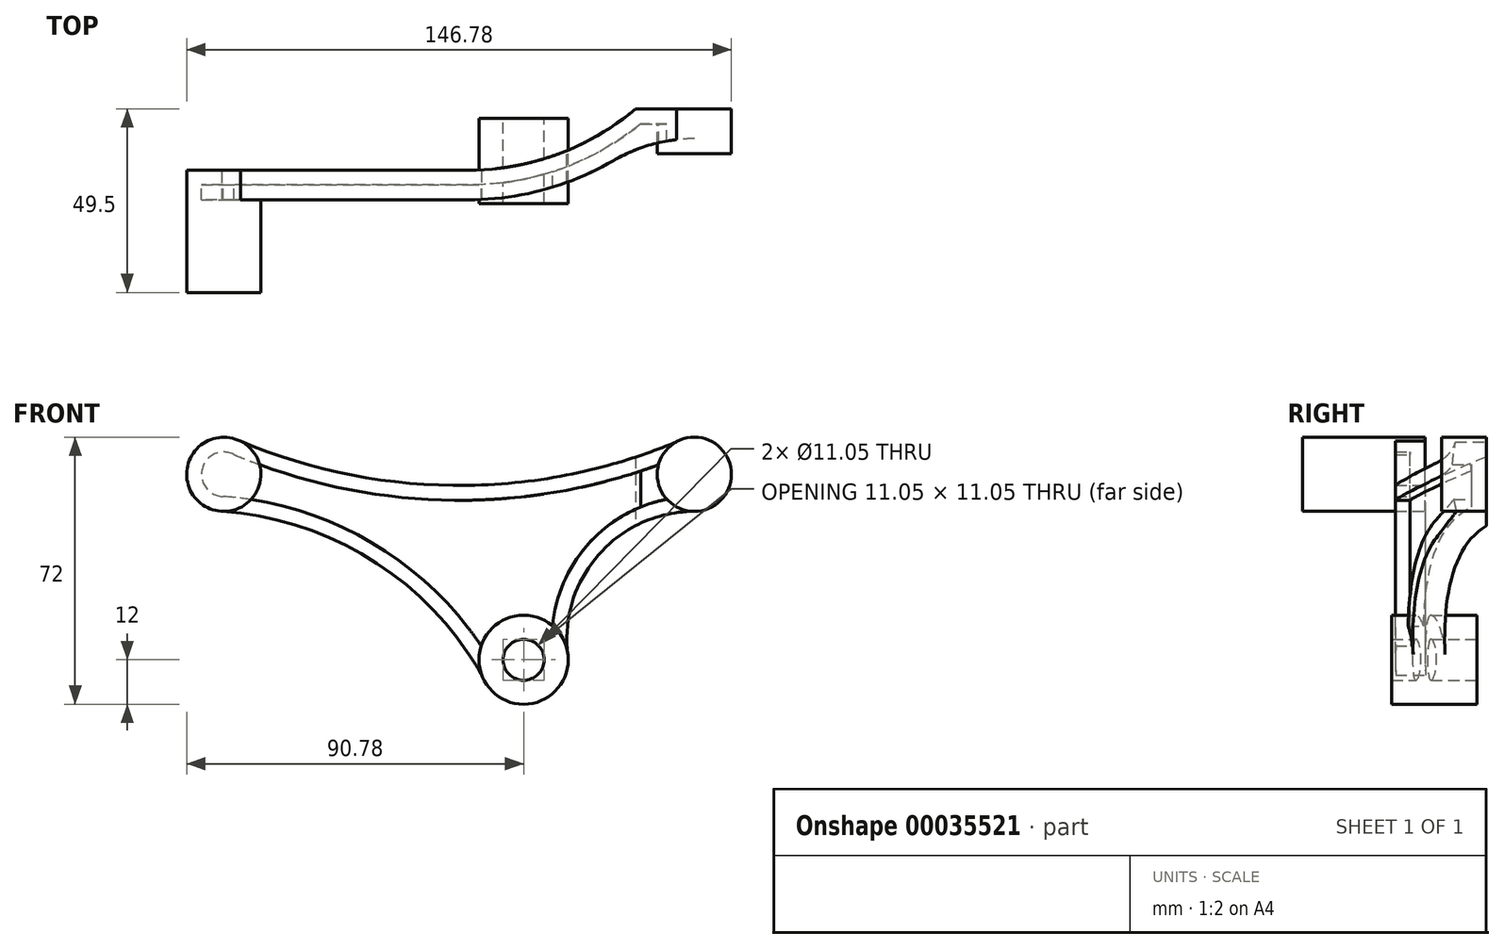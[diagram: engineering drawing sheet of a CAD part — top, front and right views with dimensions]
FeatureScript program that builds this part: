
annotation { "Feature Type Name" : "Feature", "Feature Type Description" : "" }
export const myFeature = defineFeature(function(context is Context, id is Id, definition is map)
    precondition{}
    {
        {
            var Q0;
            Q0=qCreatedBy(makeId("Front.planeOp"),FACE);
            var sketch = newSketch(context, id + "F0", { "sketchPlane" : qUnion([Q0])});
            skLineSegment(sketch, "E0", {"start": v(0, 0) * mm, "end": v(-80.78, 50) * mm, "construction": true});
            skLineSegment(sketch, "E1", {"start": v(-80.78, 50) * mm, "end": v(46, 50) * mm, "construction": true});
            skLineSegment(sketch, "E2", {"start": v(46, 50) * mm, "end": v(0, 0) * mm, "construction": true});
            skCircle(sketch, "E3", {"center": v(-80.78, 50) * mm, "radius": 6 * mm});
            skCircle(sketch, "E4", {"center": v(46, 50) * mm, "radius": 6 * mm});
            skCircle(sketch, "E5", {"center": v(0, 0) * mm, "radius": 6 * mm});
            skCircle(sketch, "E6", {"center": v(0, 0) * mm, "radius": 12 * mm});
            skCircle(sketch, "E7", {"center": v(-80.78, 50) * mm, "radius": 10 * mm});
            skCircle(sketch, "E8", {"center": v(46, 50) * mm, "radius": 10 * mm});
            skArc(sketch, "E9", {"start": v(-76.31, 58.95) * mm, "mid": v(-17.58, 47) * mm, "end": v(41.2, 58.77) * mm});
            skArc(sketch, "E10", {"start": v(46, 40) * mm, "mid": v(20.27, 28.41) * mm, "end": v(11.91, 1.46) * mm});
            skLineSegment(sketch, "E11", {"start": v(53.56, 43.45) * mm, "end": v(9.07, -7.86) * mm, "construction": true});
            skArc(sketch, "E12", {"start": v(-11.25, -4.17) * mm, "mid": v(-40.65, 26.72) * mm, "end": v(-81.16, 40) * mm});
            skSolve(sketch);
        }
        {
            var Q0;
            Q0=makeQuery(id+"F0.imprint","IMPRINT",FACE,{"disambiguationData":[TD([[makeQuery(id+"F0.imprint","IMPRINT",EDGE,{"derivedFrom":sQuery(id+"F0.wireOp",EDGE,"E3")}),1.0]])]});
            var Q1;
            Q1=makeQuery(id+"F0.imprint","IMPRINT",FACE,{"disambiguationData":[TD([[makeQuery(id+"F0.imprint","IMPRINT",EDGE,{"derivedFrom":sQuery(id+"F0.wireOp",EDGE,"E4")}),1.0]])]});
            var Q2;
            Q2=makeQuery(id+"F0.imprint","IMPRINT",FACE,{"disambiguationData":[TD([[makeQuery(id+"F0.imprint","IMPRINT",EDGE,{"derivedFrom":sQuery(id+"F0.wireOp",EDGE,"E5")}),1.0]])]});
            var Q3;
            Q3=makeQuery(id+"F0.imprint","IMPRINT",FACE,{"disambiguationData":[TD([[makeQuery(id+"F0.imprint","IMPRINT",EDGE,{"derivedFrom":sQuery(id+"F0.wireOp",EDGE,"E3")}),-1.0]])]});
            var Q4;
            Q4=makeQuery(id+"F0.imprint","IMPRINT",FACE,{"disambiguationData":[TD([[makeQuery(id+"F0.imprint","IMPRINT",EDGE,{"derivedFrom":sQuery(id+"F0.wireOp",EDGE,"E4")}),-1.0]])]});
            var Q5;
            Q5=makeQuery(id+"F0.imprint","IMPRINT",FACE,{"disambiguationData":[TD([[makeQuery(id+"F0.imprint","IMPRINT",EDGE,{"derivedFrom":sQuery(id+"F0.wireOp",EDGE,"E5")}),-1.0]])]});
            var Q6;
            {var subQ2=sQuery(id+"F0.wireOp",EDGE,"E9");Q6=makeQuery(id+"F0.imprint","IMPRINT",FACE,{"disambiguationData":[TD([[makeQuery(id+"F0.imprint","IMPRINT",EDGE,{"derivedFrom":subQ2}),-1.0]])]});}
            extrude(context, id + "F1", {"entities" : qUnion([Q0, Q1, Q2, Q3, Q4, Q5, Q6]), "depth" : 22 * mm});
        }
        {
            var Q0;
            Q0=makeQuery(id+"F1.opExtrude","CAP_FACE",FACE,{"disambiguationData":[OSD([sQuery(id+"F0.wireOp",EDGE,"E6"),sQuery(id+"F0.wireOp",EDGE,"E7"),sQuery(id+"F0.wireOp",EDGE,"E8"),sQuery(id+"F0.wireOp",EDGE,"E9"),sQuery(id+"F0.wireOp",EDGE,"E10"),sQuery(id+"F0.wireOp",EDGE,"867fa028-4eec-4aa7-8bf0-057ba3709197")])],"isStart":true});
            extrude(context, id + "F2", {"entities" : qUnion([Q0]), "operationType" : NewBodyOperationType.ADD, "depth" : 2.5 * mm});
        }
        {
            var Q0;
            Q0=qCreatedBy(makeId("Top.planeOp"),FACE);
            var sketch = newSketch(context, id + "F3", { "sketchPlane" : qUnion([Q0])});
            skLineSegment(sketch, "E13", {"start": v(39.84, 12.5) * mm, "end": v(-100, 12.5) * mm});
            skLineSegment(sketch, "E14", {"start": v(-100, 12.5) * mm, "end": v(-100, -14) * mm});
            skLineSegment(sketch, "E15", {"start": v(-100, -14) * mm, "end": v(-15, -14) * mm});
            skLineSegment(sketch, "E16", {"start": v(-15, -22) * mm, "end": v(-15, -25.86) * mm});
            skLineSegment(sketch, "E17", {"start": v(-15, -25.86) * mm, "end": v(70, -25.86) * mm});
            skLineSegment(sketch, "E18", {"start": v(70, -25.86) * mm, "end": v(70, -5.5) * mm});
            skLineSegment(sketch, "E19", {"start": v(70, -5.5) * mm, "end": v(46.12, -5.5) * mm});
            skArc(sketch, "E20", {"start": v(-15, -14) * mm, "mid": v(15.45, -7.03) * mm, "end": v(39.84, 12.5) * mm});
            skArc(sketch, "E21.0", {"start": v(-15, -22) * mm, "mid": v(5.33, -19.3) * mm, "end": v(24.25, -11.4) * mm});
            skPoint(sketch, "E22.visualSharp", {"position": v(32.98, -5.5) * mm});
            skArc(sketch, "E22.filletArc", {"start": v(46.12, -5.5) * mm, "mid": v(34.8, -7) * mm, "end": v(24.25, -11.4) * mm});
            skSolve(sketch);
        }
        {
            var Q0;
            Q0=makeQuery(id+"F3.imprint","IMPRINT",FACE,{"disambiguationData":[TD([[makeQuery(id+"F3.imprint","IMPRINT",EDGE,{"derivedFrom":sQuery(id+"F3.wireOp",EDGE,"E13")}),1.0]])]});
            var Q1;
            Q1=makeQuery(id+"F3.imprint","IMPRINT",FACE,{"disambiguationData":[TD([[makeQuery(id+"F3.imprint","IMPRINT",EDGE,{"derivedFrom":sQuery(id+"F3.wireOp",EDGE,"E16")}),1.0]])]});
            extrude(context, id + "F4", {"entities" : qUnion([Q0, Q1]), "operationType" : NewBodyOperationType.REMOVE, "endBound" : BoundingType.SYMMETRIC, "depth" : 211 * mm});
        }
        {
            var Q0;
            Q0=makeQuery(id+"F3.imprint","IMPRINT",FACE,{"disambiguationData":[TD([[makeQuery(id+"F3.imprint","IMPRINT",EDGE,{"derivedFrom":sQuery(id+"F3.wireOp",EDGE,"E16")}),1.0]])]});
            extrude(context, id + "F5", {"entities" : qUnion([Q0]), "operationType" : NewBodyOperationType.REMOVE, "endBound" : BoundingType.THROUGH_ALL, "oppositeDirection" : true, "depth" : 25 * mm});
        }
        {
            var Q0;
            Q0=makeQuery(id+"F1.opExtrude","CAP_FACE",FACE,{"disambiguationData":[OSD([sQuery(id+"F0.wireOp",EDGE,"E6"),sQuery(id+"F0.wireOp",EDGE,"E7"),sQuery(id+"F0.wireOp",EDGE,"E8"),sQuery(id+"F0.wireOp",EDGE,"E9"),sQuery(id+"F0.wireOp",EDGE,"E10"),sQuery(id+"F0.wireOp",EDGE,"E12")])],"isStart":false});
            var Q1;
            Q1=makeQuery(id+"F4.boolean.opBoolean","COPY",FACE,{"derivedFrom":makeQuery(id+"F4.opExtrude","SWEPT_FACE",FACE,{"disambiguationData":[OSD([sQuery(id+"F3.wireOp",EDGE,"E22.filletArc")])]})});
            var Q2;
            Q2=makeQuery(id+"F4.boolean.opBoolean","COPY",FACE,{"derivedFrom":makeQuery(id+"F4.opExtrude","SWEPT_FACE",FACE,{"disambiguationData":[OSD([sQuery(id+"F3.wireOp",EDGE,"E19")])]})});
            var Q3;
            Q3=makeQuery(id+"F4.boolean.opBoolean","COPY",FACE,{"derivedFrom":makeQuery(id+"F4.opExtrude","SWEPT_FACE",FACE,{"disambiguationData":[OSD([sQuery(id+"F3.wireOp",EDGE,"E21.0")])]})});
            shell(context, id + "F6", {"entities" : qUnion([Q0, Q1, Q2, Q3]), "thickness" : 4 * mm});
        }
        {
            var Q0;
            Q0=qCreatedBy(makeId("Front.planeOp"),FACE);
            var sketch = newSketch(context, id + "F7", { "sketchPlane" : qUnion([Q0])});
            skCircle(sketch, "E23", {"center": v(0, 0) * mm, "radius": 5.52 * mm});
            skCircle(sketch, "E24", {"center": v(0, 0) * mm, "radius": 12 * mm});
            skSolve(sketch);
        }
        {
            var Q0;
            Q0 = qSketchRegion(id + "F7", true);
            extrude(context, id + "F8", {"entities" : qUnion([Q0]), "operationType" : NewBodyOperationType.ADD, "depth" : 23 * mm});
        }
        {
            var Q0;
            Q0=makeQuery(id+"F4.boolean.opBoolean","COPY",FACE,{"derivedFrom":makeQuery(id+"F4.opExtrude","SWEPT_FACE",FACE,{"disambiguationData":[OSD([sQuery(id+"F3.wireOp",EDGE,"E19")])]})});
            var sketch = newSketch(context, id + "F9", { "sketchPlane" : qUnion([Q0])});
            skCircle(sketch, "E25", {"center": v(46, 50) * mm, "radius": 10 * mm});
            skSolve(sketch);
        }
        {
            var Q0;
            Q0 = qSketchRegion(id + "F9", true);
            extrude(context, id + "F10", {"entities" : qUnion([Q0]), "operationType" : NewBodyOperationType.ADD, "endBound" : BoundingType.SYMMETRIC, "depth" : 8 * mm});
        }
        {
            var Q0;
            Q0=makeQuery(id+"F1.opExtrude","CAP_FACE",FACE,{"disambiguationData":[OSD([sQuery(id+"F0.wireOp",EDGE,"E6"),sQuery(id+"F0.wireOp",EDGE,"E7"),sQuery(id+"F0.wireOp",EDGE,"E8"),sQuery(id+"F0.wireOp",EDGE,"E9"),sQuery(id+"F0.wireOp",EDGE,"E10"),sQuery(id+"F0.wireOp",EDGE,"E12")])],"isStart":false});
            var sketch = newSketch(context, id + "F11", { "sketchPlane" : qUnion([Q0])});
            skCircle(sketch, "E26", {"center": v(-80.78, 50) * mm, "radius": 10 * mm});
            skSolve(sketch);
        }
        {
            var Q0;
            Q0 = qSketchRegion(id + "F11", true);
            extrude(context, id + "F12", {"entities" : qUnion([Q0]), "operationType" : NewBodyOperationType.ADD, "depth" : 25 * mm});
        }
    });
